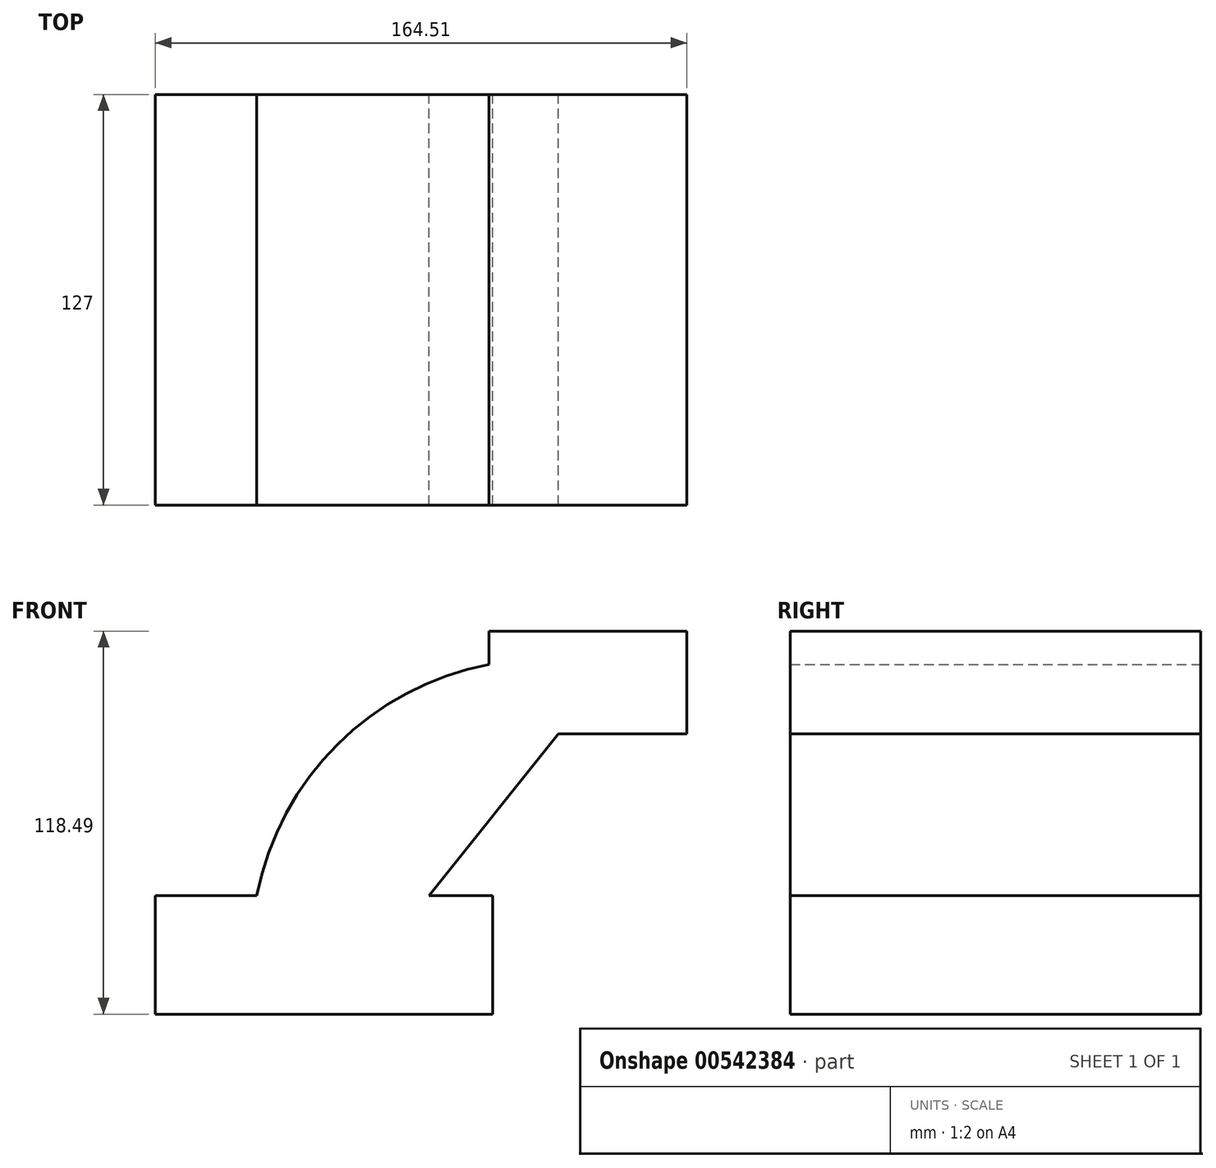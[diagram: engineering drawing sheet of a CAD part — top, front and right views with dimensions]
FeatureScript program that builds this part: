
annotation { "Feature Type Name" : "Feature", "Feature Type Description" : "" }
export const myFeature = defineFeature(function(context is Context, id is Id, definition is map)
    precondition{}
    {
        {
            var Q0;
            Q0=qCreatedBy(makeId("Front.planeOp"),FACE);
            var sketch = newSketch(context, id + "F0", { "sketchPlane" : qUnion([Q0])});
            skLineSegment(sketch, "E0.bottom", {"start": v(-50.66, -15.36) * mm, "end": v(53.73, -15.36) * mm});
            skLineSegment(sketch, "E0.top", {"start": v(-50.66, -51.98) * mm, "end": v(53.73, -51.98) * mm});
            skLineSegment(sketch, "E0.left", {"start": v(-50.66, -15.36) * mm, "end": v(-50.66, -51.98) * mm});
            skLineSegment(sketch, "E0.right", {"start": v(53.73, -15.36) * mm, "end": v(53.73, -51.98) * mm});
            skLineSegment(sketch, "E1.bottom", {"start": v(52.58, 66.5) * mm, "end": v(113.85, 66.5) * mm});
            skLineSegment(sketch, "E1.top", {"start": v(52.58, 34.68) * mm, "end": v(113.85, 34.68) * mm});
            skLineSegment(sketch, "E1.left", {"start": v(52.58, 66.5) * mm, "end": v(52.58, 34.68) * mm});
            skLineSegment(sketch, "E1.right", {"start": v(113.85, 66.5) * mm, "end": v(113.85, 34.68) * mm});
            skLineSegment(sketch, "E2", {"start": v(19.04, -34.12) * mm, "end": v(81.67, 44.26) * mm});
            skArc(sketch, "E3", {"start": v(57.03, 56.92) * mm, "mid": v(4.75, 30.48) * mm, "end": v(-20.32, -22.48) * mm});
            skSolve(sketch);
        }
        {
            var Q0;
            Q0=makeQuery(id+"F0.imprint","IMPRINT",FACE,{"disambiguationData":[TD([[makeQuery(id+"F0.imprint","IMPRINT",EDGE,{"derivedFrom":sQuery(id+"F0.wireOp",EDGE,"E0.top")}),1.0]])]});
            var Q1;
            {var subQ3=sQuery(id+"F0.wireOp",EDGE,"E3");var subQ6=sQuery(id+"F0.wireOp",EDGE,"E0.bottom");var subQ9=makeQuery(id+"F0.imprint","INTERSECT",VERTEX,{"derivedFrom":[subQ6,subQ3]});Q1=makeQuery(id+"F0.imprint","IMPRINT",FACE,{"disambiguationData":[TD([[makeQuery(id+"F0.imprint","IMPRINT",EDGE,{"disambiguationData":[TD([[subQ9,-1.0]])],"derivedFrom":subQ6}),1.0]])]});}
            var Q2;
            {var subQ1=sQuery(id+"F0.wireOp",EDGE,"E1.bottom");Q2=makeQuery(id+"F0.imprint","IMPRINT",FACE,{"disambiguationData":[TD([[makeQuery(id+"F0.imprint","IMPRINT",EDGE,{"derivedFrom":subQ1}),-1.0]])]});}
            extrude(context, id + "F1", {"entities" : qUnion([Q0, Q1, Q2]), "endBound" : BoundingType.SYMMETRIC, "depth" : 127 * mm, "offsetDistance" : 25.4 * mm});
        }
    });
